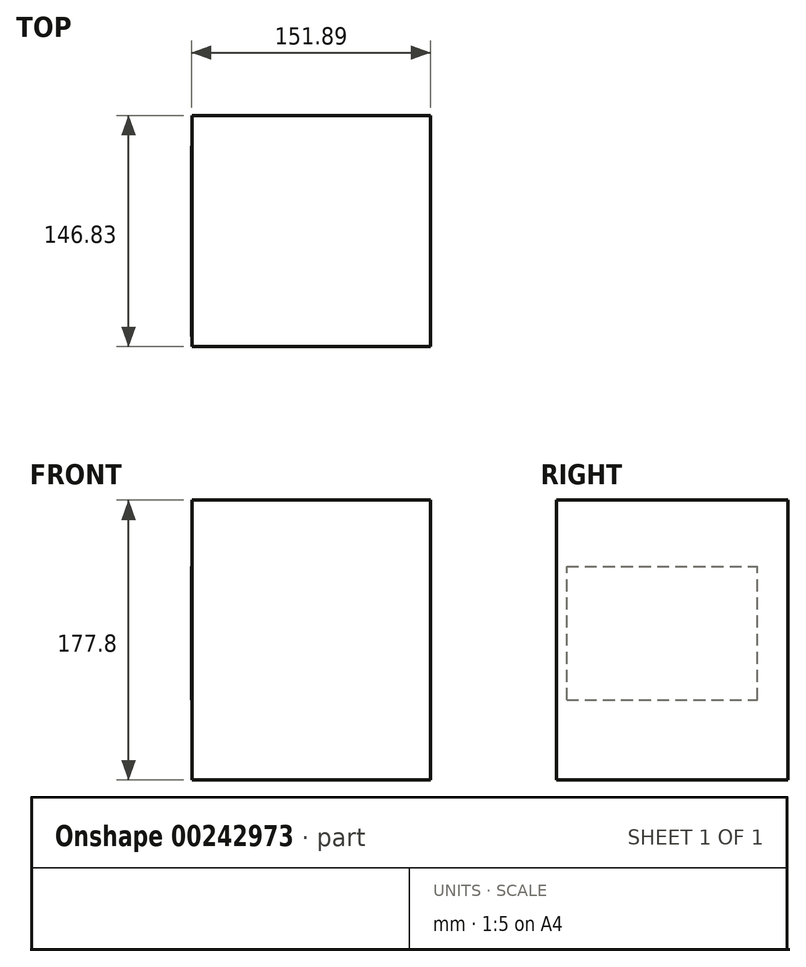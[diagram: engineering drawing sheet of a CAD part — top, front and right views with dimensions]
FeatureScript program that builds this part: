
annotation { "Feature Type Name" : "Feature", "Feature Type Description" : "" }
export const myFeature = defineFeature(function(context is Context, id is Id, definition is map)
    precondition{}
    {
        {
            var Q0;
            Q0=qCreatedBy(makeId("Top.planeOp"),FACE);
            var sketch = newSketch(context, id + "F0", { "sketchPlane" : qUnion([Q0])});
            skLineSegment(sketch, "E0.bottom", {"start": v(-47.92, 64.52) * mm, "end": v(103.62, 64.52) * mm});
            skLineSegment(sketch, "E0.top", {"start": v(-47.92, -82.3) * mm, "end": v(103.62, -82.3) * mm});
            skLineSegment(sketch, "E0.left", {"start": v(-47.92, 64.52) * mm, "end": v(-47.92, -82.3) * mm});
            skLineSegment(sketch, "E0.right", {"start": v(103.62, 64.52) * mm, "end": v(103.62, -82.3) * mm});
            skSolve(sketch);
        }
        {
            var Q0;
            Q0 = qSketchRegion(id + "F0", true);
            extrude(context, id + "F1", {"entities" : qUnion([Q0]), "depth" : 177.8 * mm});
        }
        {
            var Q0;
            Q0=makeQuery(id+"F1.opExtrude","SWEPT_FACE",FACE,{"disambiguationData":[OSD([sQuery(id+"F0.wireOp",EDGE,"E0.left")])]});
            var sketch = newSketch(context, id + "F2", { "sketchPlane" : qUnion([Q0])});
            skLineSegment(sketch, "E1", {"start": v(-31.45, 103.96) * mm, "end": v(31.9, 103.96) * mm});
            skLineSegment(sketch, "E2", {"start": v(31.9, 103.96) * mm, "end": v(31.9, 0) * mm});
            skLineSegment(sketch, "E3", {"start": v(31.9, 0) * mm, "end": v(-29.36, 0) * mm});
            skLineSegment(sketch, "E4", {"start": v(-29.36, 0) * mm, "end": v(-31.45, 103.96) * mm});
            skSolve(sketch);
        }
        {
            var Q0;
            Q0 = qSketchRegion(id + "F2", true);
            extrude(context, id + "F3", {"entities" : qUnion([Q0]), "operationType" : NewBodyOperationType.ADD, "oppositeDirection" : true, "depth" : 38.1 * mm});
        }
        {
            var Q0;
            Q0=makeQuery(id+"F1.opExtrude","SWEPT_FACE",FACE,{"disambiguationData":[OSD([sQuery(id+"F0.wireOp",EDGE,"E0.right")])]});
            var sketch = newSketch(context, id + "F4", { "sketchPlane" : qUnion([Q0])});
            skLineSegment(sketch, "E5.bottom", {"start": v(-55.89, 155.23) * mm, "end": v(44.7, 155.23) * mm});
            skLineSegment(sketch, "E5.top", {"start": v(-55.89, 26.01) * mm, "end": v(44.7, 26.01) * mm});
            skLineSegment(sketch, "E5.left", {"start": v(-55.89, 155.23) * mm, "end": v(-55.89, 26.01) * mm});
            skLineSegment(sketch, "E5.right", {"start": v(44.7, 155.23) * mm, "end": v(44.7, 26.01) * mm});
            skSolve(sketch);
        }
        {
            var Q0;
            Q0 = qSketchRegion(id + "F4", true);
            extrude(context, id + "F5", {"entities" : qUnion([Q0]), "operationType" : NewBodyOperationType.ADD, "oppositeDirection" : true, "depth" : 25.4 * mm});
        }
        {
            var Q0;
            Q0=makeQuery(id+"F1.opExtrude","SWEPT_FACE",FACE,{"disambiguationData":[OSD([sQuery(id+"F0.wireOp",EDGE,"E0.right")])]});
            var sketch = newSketch(context, id + "F6", { "sketchPlane" : qUnion([Q0])});
            skLineSegment(sketch, "E6.bottom", {"start": v(-75.94, 50.9) * mm, "end": v(45.11, 50.9) * mm});
            skLineSegment(sketch, "E6.top", {"start": v(-75.94, 135.55) * mm, "end": v(45.11, 135.55) * mm});
            skLineSegment(sketch, "E6.left", {"start": v(-75.94, 50.9) * mm, "end": v(-75.94, 135.55) * mm});
            skLineSegment(sketch, "E6.right", {"start": v(45.11, 50.9) * mm, "end": v(45.11, 135.55) * mm});
            skSolve(sketch);
        }
        {
            var Q0;
            Q0=makeQuery(id+"F6.imprint","IMPRINT",FACE,{"disambiguationData":[TD([[makeQuery(id+"F6.imprint","IMPRINT",EDGE,{"derivedFrom":sQuery(id+"F6.wireOp",EDGE,"E6.bottom")}),1.0]])]});
            extrude(context, id + "F7", {"entities" : qUnion([Q0]), "operationType" : NewBodyOperationType.ADD, "oppositeDirection" : true, "depth" : 151.9 * mm});
        }
    });
